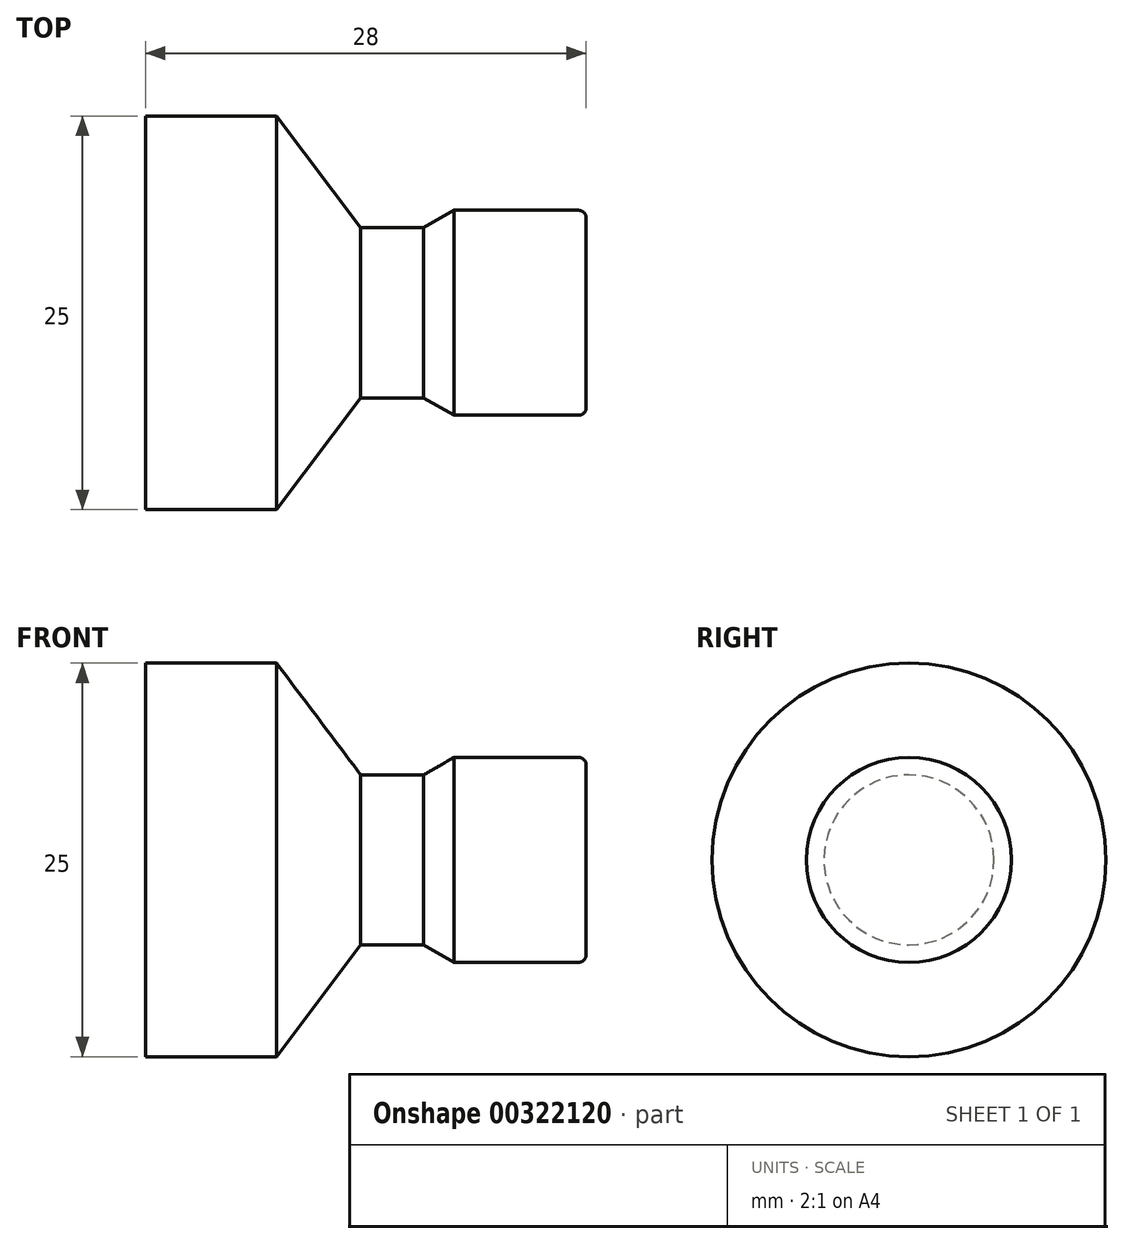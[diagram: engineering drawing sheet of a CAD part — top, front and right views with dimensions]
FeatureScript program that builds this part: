
annotation { "Feature Type Name" : "Feature", "Feature Type Description" : "" }
export const myFeature = defineFeature(function(context is Context, id is Id, definition is map)
    precondition{}
    {
        {
            var Q0;
            Q0=qCreatedBy(makeId("Front.planeOp"),FACE);
            var sketch = newSketch(context, id + "F0", { "sketchPlane" : qUnion([Q0])});
            skLineSegment(sketch, "E0", {"start": v(0, 0) * mm, "end": v(0, 6) * mm});
            skLineSegment(sketch, "E1", {"start": v(-0.5, 6.5) * mm, "end": v(-8.4, 6.5) * mm});
            skLineSegment(sketch, "E2", {"start": v(-8.4, 6.5) * mm, "end": v(-8.4, 0) * mm});
            skLineSegment(sketch, "E3", {"start": v(-8.4, 0) * mm, "end": v(0, 0) * mm});
            skLineSegment(sketch, "E4", {"start": v(-8.4, 6.5) * mm, "end": v(-10.32, 5.4) * mm});
            skLineSegment(sketch, "E5", {"start": v(-10.32, 5.4) * mm, "end": v(-10.32, 0) * mm});
            skLineSegment(sketch, "E6", {"start": v(-28, 0) * mm, "end": v(-28, 12.5) * mm});
            skLineSegment(sketch, "E7", {"start": v(-28, 0) * mm, "end": v(0, 0) * mm});
            skLineSegment(sketch, "E8", {"start": v(-28, 12.5) * mm, "end": v(-19.67, 12.5) * mm});
            skLineSegment(sketch, "E9", {"start": v(-19.67, 12.5) * mm, "end": v(-19.67, 0) * mm});
            skLineSegment(sketch, "E10", {"start": v(-19.67, 12.5) * mm, "end": v(-14.32, 5.4) * mm});
            skLineSegment(sketch, "E11", {"start": v(-10.32, 5.4) * mm, "end": v(-14.32, 5.4) * mm});
            skPoint(sketch, "E12.visualSharp", {"position": v(0, 6.5) * mm});
            skArc(sketch, "E12.filletArc", {"start": v(0, 6) * mm, "mid": v(-0.15, 6.36) * mm, "end": v(-0.5, 6.5) * mm});
            skSolve(sketch);
        }
        {
            var Q0;
            {var subQ1=sQuery(id+"F0.wireOp",EDGE,"E0");Q0=makeQuery(id+"F0.imprint","IMPRINT",FACE,{"disambiguationData":[TD([[makeQuery(id+"F0.imprint","IMPRINT",EDGE,{"derivedFrom":subQ1}),1.0]])]});}
            var Q1;
            {var subQ0=sQuery(id+"F0.wireOp",EDGE,"E2");Q1=makeQuery(id+"F0.imprint","IMPRINT",FACE,{"disambiguationData":[TD([[makeQuery(id+"F0.imprint","IMPRINT",EDGE,{"derivedFrom":subQ0}),-1.0]])]});}
            var Q2;
            {var subQ2=sQuery(id+"F0.wireOp",EDGE,"E5");Q2=makeQuery(id+"F0.imprint","IMPRINT",FACE,{"disambiguationData":[TD([[makeQuery(id+"F0.imprint","IMPRINT",EDGE,{"derivedFrom":subQ2}),-1.0]])]});}
            var Q3;
            {var subQ0=sQuery(id+"F0.wireOp",EDGE,"E6");Q3=makeQuery(id+"F0.imprint","IMPRINT",FACE,{"disambiguationData":[TD([[makeQuery(id+"F0.imprint","IMPRINT",EDGE,{"derivedFrom":subQ0}),-1.0]])]});}
            var Q4;
            Q4=sQuery(id+"F0.wireOp",EDGE,"E7");
            revolve(context, id + "F1", {"entities" : qUnion([Q0, Q1, Q2, Q3]), "axis" : qUnion([Q4]), "revolveType" : RevolveType.FULL});
        }
    });
